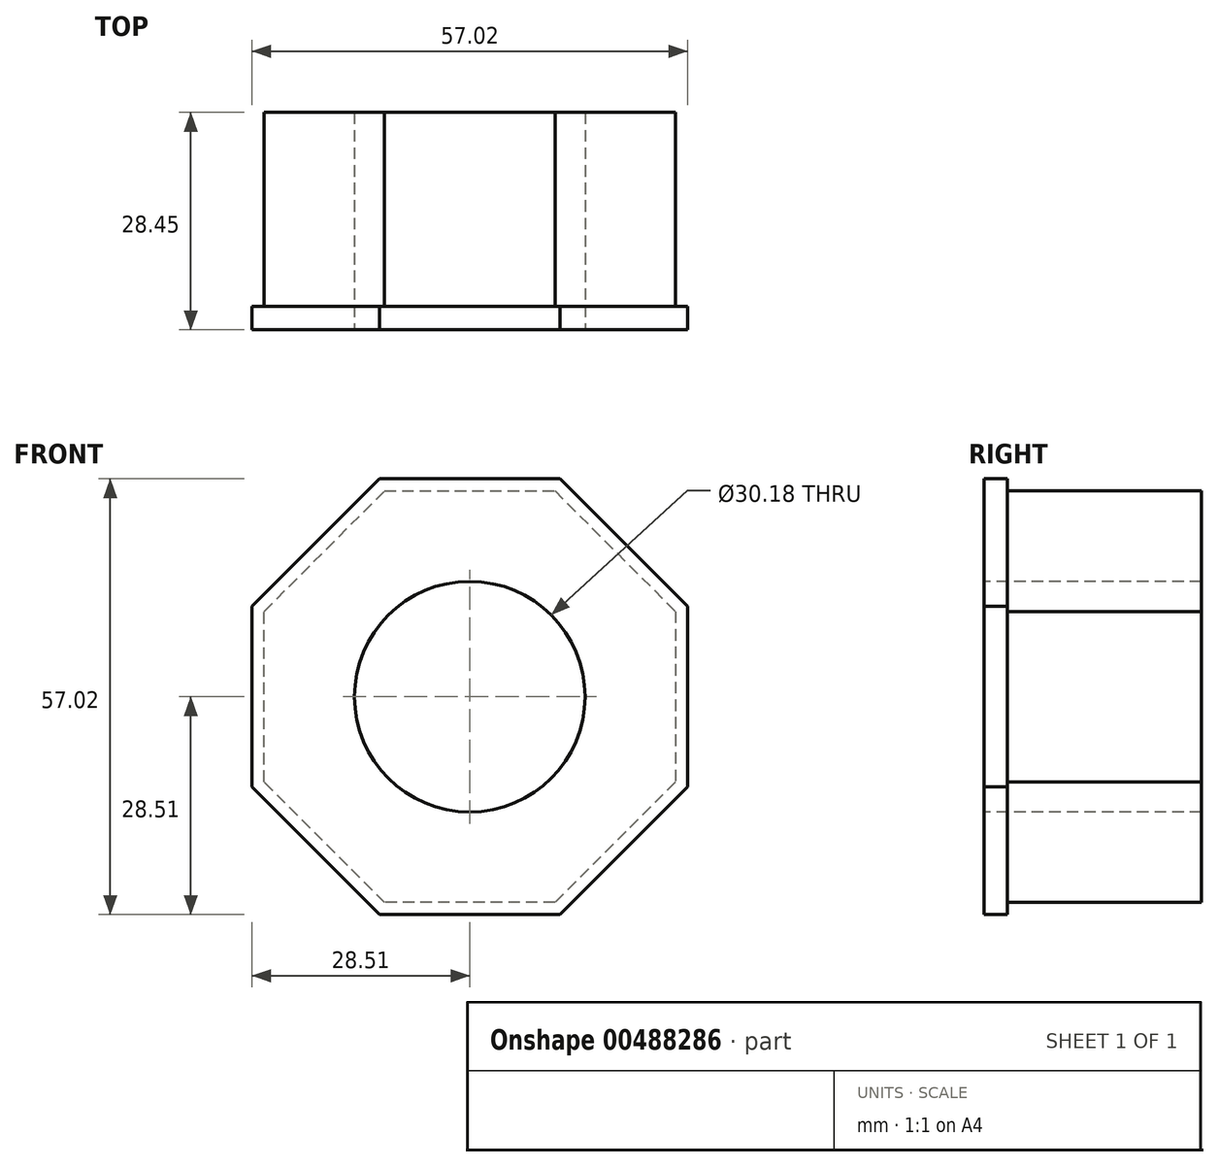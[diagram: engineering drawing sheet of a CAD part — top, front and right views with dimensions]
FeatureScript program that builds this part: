
annotation { "Feature Type Name" : "Feature", "Feature Type Description" : "" }
export const myFeature = defineFeature(function(context is Context, id is Id, definition is map)
    precondition{}
    {
        {
            var Q0;
            Q0=qCreatedBy(makeId("Front.planeOp"),FACE);
            var sketch = newSketch(context, id + "F0", { "sketchPlane" : qUnion([Q0])});
            skCircle(sketch, "E0.cCircle", {"center": v(0, 0) * mm, "radius": 26.92 * mm, "construction": true});
            skLineSegment(sketch, "E0.0", {"start": v(-11.15, 26.92) * mm, "end": v(11.15, 26.92) * mm});
            skLineSegment(sketch, "E0.1", {"start": v(11.15, 26.92) * mm, "end": v(26.92, 11.15) * mm});
            skLineSegment(sketch, "E0.2", {"start": v(26.92, 11.15) * mm, "end": v(26.92, -11.15) * mm});
            skLineSegment(sketch, "E0.3", {"start": v(26.92, -11.15) * mm, "end": v(11.15, -26.92) * mm});
            skLineSegment(sketch, "E0.4", {"start": v(11.15, -26.92) * mm, "end": v(-11.15, -26.92) * mm});
            skLineSegment(sketch, "E0.5", {"start": v(-11.15, -26.92) * mm, "end": v(-26.92, -11.15) * mm});
            skLineSegment(sketch, "E0.6", {"start": v(-26.92, -11.15) * mm, "end": v(-26.92, 11.15) * mm});
            skLineSegment(sketch, "E0.7", {"start": v(-26.92, 11.15) * mm, "end": v(-11.15, 26.92) * mm});
            skPoint(sketch, "E0.0.midPoint", {"position": v(0, 26.92) * mm});
            skSolve(sketch);
        }
        {
            var Q0;
            Q0 = qSketchRegion(id + "F0", true);
            extrude(context, id + "F1", {"entities" : qUnion([Q0]), "depth" : 25.4 * mm});
        }
        {
            var Q0;
            Q0=makeQuery(id+"F1.opExtrude","CAP_FACE",FACE,{"disambiguationData":[OSD([sQuery(id+"F0.wireOp",EDGE,"E0.0"),sQuery(id+"F0.wireOp",EDGE,"E0.1"),sQuery(id+"F0.wireOp",EDGE,"E0.2"),sQuery(id+"F0.wireOp",EDGE,"E0.3"),sQuery(id+"F0.wireOp",EDGE,"E0.4"),sQuery(id+"F0.wireOp",EDGE,"E0.5"),sQuery(id+"F0.wireOp",EDGE,"E0.6"),sQuery(id+"F0.wireOp",EDGE,"E0.7")])],"isStart":false});
            var sketch = newSketch(context, id + "F2", { "sketchPlane" : qUnion([Q0])});
            skCircle(sketch, "E1.cCircle", {"center": v(0, 0) * mm, "radius": 28.51 * mm, "construction": true});
            skPoint(sketch, "E1.cCircle.perimeterSnap0", {"position": v(0, 26.92) * mm});
            skLineSegment(sketch, "E1.0", {"start": v(-11.8, 28.51) * mm, "end": v(11.8, 28.51) * mm});
            skLineSegment(sketch, "E1.1", {"start": v(11.8, 28.51) * mm, "end": v(28.51, 11.8) * mm});
            skLineSegment(sketch, "E1.2", {"start": v(28.51, 11.8) * mm, "end": v(28.51, -11.8) * mm});
            skLineSegment(sketch, "E1.3", {"start": v(28.51, -11.8) * mm, "end": v(11.8, -28.51) * mm});
            skLineSegment(sketch, "E1.4", {"start": v(11.8, -28.51) * mm, "end": v(-11.8, -28.51) * mm});
            skLineSegment(sketch, "E1.5", {"start": v(-11.8, -28.51) * mm, "end": v(-28.51, -11.8) * mm});
            skLineSegment(sketch, "E1.6", {"start": v(-28.51, -11.8) * mm, "end": v(-28.51, 11.8) * mm});
            skLineSegment(sketch, "E1.7", {"start": v(-28.51, 11.8) * mm, "end": v(-11.8, 28.51) * mm});
            skPoint(sketch, "E1.0.midPoint", {"position": v(0, 28.51) * mm});
            skPoint(sketch, "E1.0.midPoint.positionSnap0", {"position": v(0, 26.92) * mm});
            skSolve(sketch);
        }
        {
            var Q0;
            Q0 = qSketchRegion(id + "F2", true);
            extrude(context, id + "F3", {"entities" : qUnion([Q0]), "operationType" : NewBodyOperationType.ADD, "depth" : 3.05 * mm});
        }
        {
            var Q0;
            Q0=makeQuery(id+"F3.opExtrude","CAP_FACE",FACE,{"disambiguationData":[OSD([sQuery(id+"F2.wireOp",EDGE,"E1.0"),sQuery(id+"F2.wireOp",EDGE,"E1.1"),sQuery(id+"F2.wireOp",EDGE,"E1.2"),sQuery(id+"F2.wireOp",EDGE,"E1.3"),sQuery(id+"F2.wireOp",EDGE,"E1.4"),sQuery(id+"F2.wireOp",EDGE,"E1.5"),sQuery(id+"F2.wireOp",EDGE,"E1.6"),sQuery(id+"F2.wireOp",EDGE,"E1.7")])],"isStart":false});
            var sketch = newSketch(context, id + "F4", { "sketchPlane" : qUnion([Q0])});
            skCircle(sketch, "E2", {"center": v(0, 0) * mm, "radius": 15.09 * mm});
            skSolve(sketch);
        }
        {
            var Q0;
            Q0 = qSketchRegion(id + "F4", true);
            extrude(context, id + "F5", {"entities" : qUnion([Q0]), "operationType" : NewBodyOperationType.REMOVE, "endBound" : BoundingType.THROUGH_ALL, "oppositeDirection" : true, "depth" : 25.4 * mm});
        }
    });
